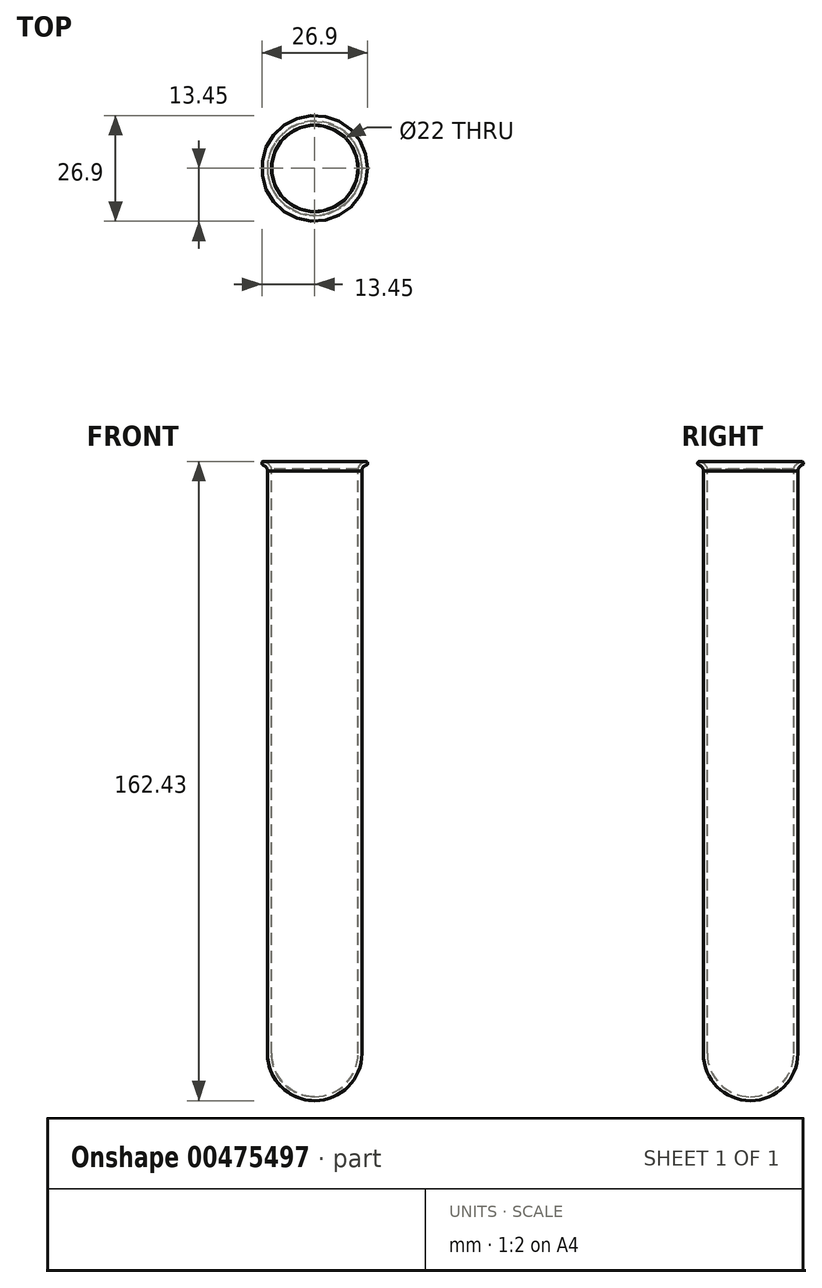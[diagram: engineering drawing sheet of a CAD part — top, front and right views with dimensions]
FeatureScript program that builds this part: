
annotation { "Feature Type Name" : "Feature", "Feature Type Description" : "" }
export const myFeature = defineFeature(function(context is Context, id is Id, definition is map)
    precondition{}
    {
        {
            var Q0;
            Q0=qCreatedBy(makeId("Front.planeOp"),FACE);
            var sketch = newSketch(context, id + "F0", { "sketchPlane" : qUnion([Q0])});
            skLineSegment(sketch, "E0", {"start": v(-12, 12) * mm, "end": v(-12, 160) * mm});
            skArc(sketch, "E1", {"start": v(-12, 12) * mm, "mid": v(-8.49, 3.51) * mm, "end": v(0, 0) * mm});
            skLineSegment(sketch, "E2", {"start": v(-11, 160.5) * mm, "end": v(-11, 12) * mm});
            skArc(sketch, "E3", {"start": v(-11, 12) * mm, "mid": v(-7.78, 4.22) * mm, "end": v(0, 1) * mm});
            skFitSpline(sketch, "E4", {"points": [v(-12, 160) * mm, v(-12.91, 161.4) * mm, v(-13.43, 161.75) * mm, v(-13.24, 162.35) * mm, v(-12.37, 162.2) * mm, v(-11, 160.5) * mm], "startDerivative": vector(1, 9.47) * mm, "endDerivative": vector(-0.39, -7.25) * mm});
            skLineSegment(sketch, "E5", {"start": v(0, 50) * mm, "end": v(0, 0) * mm, "construction": true});
            skLineSegment(sketch, "E6", {"start": v(0, 1) * mm, "end": v(0, 0) * mm});
            skSolve(sketch);
        }
        {
            var Q0;
            Q0=makeQuery(id+"F0.imprint","IMPRINT",FACE,{"disambiguationData":[TD([[makeQuery(id+"F0.imprint","IMPRINT",EDGE,{"derivedFrom":sQuery(id+"F0.wireOp",EDGE,"E0")}),-1.0]])]});
            var Q1;
            Q1=sQuery(id+"F0.wireOp",EDGE,"E5");
            revolve(context, id + "F1", {"entities" : qUnion([Q0]), "axis" : qUnion([Q1]), "revolveType" : RevolveType.FULL});
        }
    });
